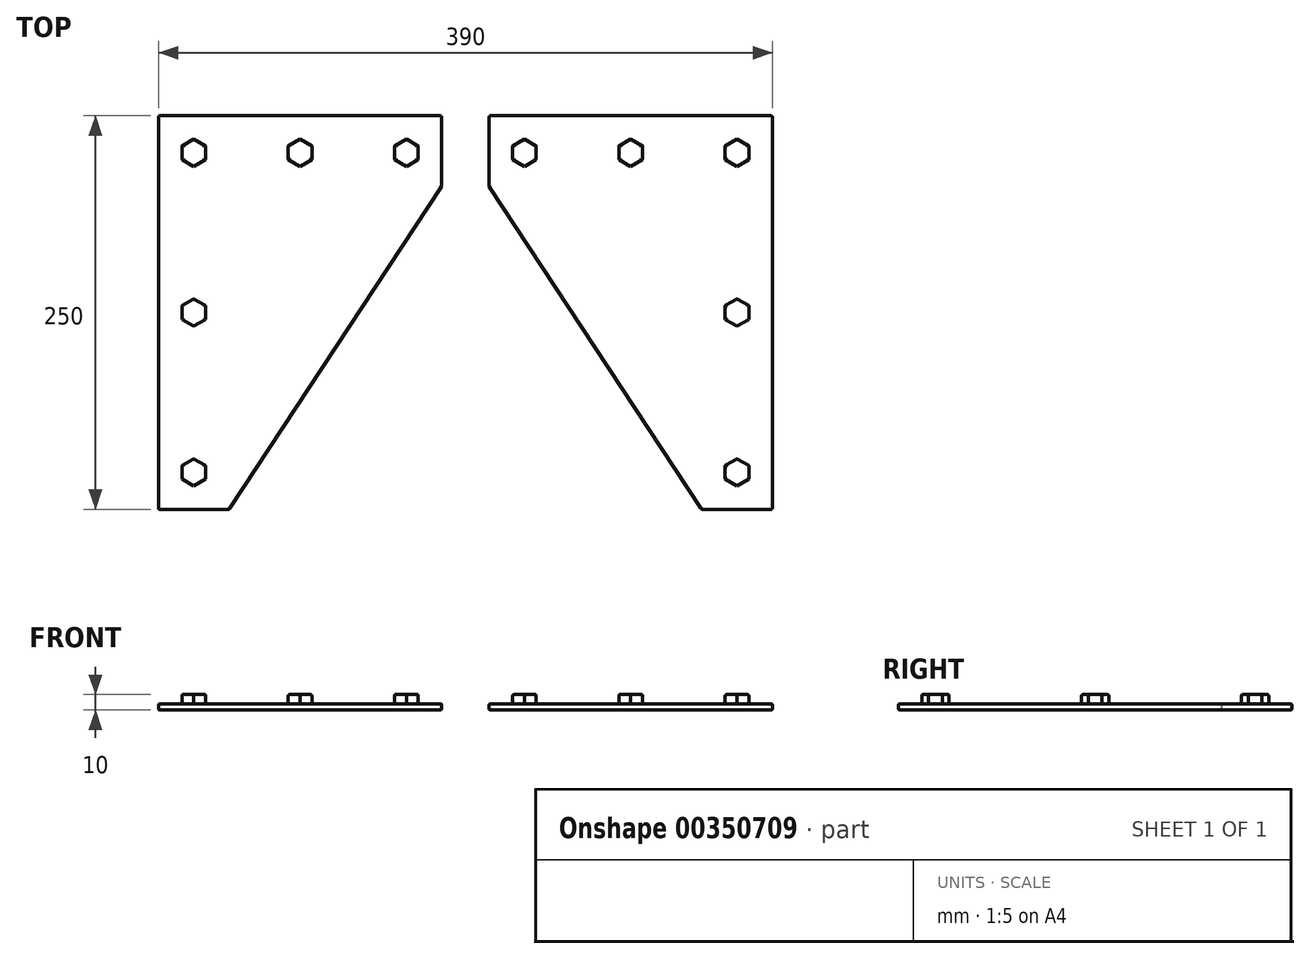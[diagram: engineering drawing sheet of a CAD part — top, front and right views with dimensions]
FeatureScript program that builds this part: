
annotation { "Feature Type Name" : "Feature", "Feature Type Description" : "" }
export const myFeature = defineFeature(function(context is Context, id is Id, definition is map)
    precondition{}
    {
        {
            var Q0;
            Q0=qCreatedBy(makeId("Top.planeOp"),FACE);
            var sketch = newSketch(context, id + "F0", { "sketchPlane" : qUnion([Q0])});
            skLineSegment(sketch, "E0", {"start": v(15, 200) * mm, "end": v(195, 200) * mm});
            skLineSegment(sketch, "E1", {"start": v(195, 200) * mm, "end": v(195, -50) * mm});
            skLineSegment(sketch, "E2", {"start": v(195, -50) * mm, "end": v(150, -50) * mm});
            skLineSegment(sketch, "E3", {"start": v(15, 200) * mm, "end": v(15, 155) * mm});
            skLineSegment(sketch, "E4", {"start": v(15, 155) * mm, "end": v(150, -50) * mm});
            skSolve(sketch);
        }
        {
            var Q0;
            Q0=qSketchRegion(id+"F0",true);
            extrude(context, id + "F1", {"entities" : qUnion([Q0]), "depth" : 4 * mm});
        }
        {
            var Q0;
            Q0=makeQuery(id+"F1.opExtrude","CAP_FACE",FACE,{"disambiguationData":[OSD([sQuery(id+"F0.wireOp",EDGE,"OxDFXuYp-wWxs-4NzO-t9D3-rnYw7JfFts5y"),sQuery(id+"F0.wireOp",EDGE,"E0"),sQuery(id+"F0.wireOp",EDGE,"E1"),sQuery(id+"F0.wireOp",EDGE,"E2")])],"isStart":false});
            var Q1;
            Q1=makeQuery(id+"F1.opExtrude","CAP_FACE",FACE,{"disambiguationData":[OSD([sQuery(id+"F0.wireOp",EDGE,"OxDFXuYp-wWxs-4NzO-t9D3-rnYw7JfFts5y"),sQuery(id+"F0.wireOp",EDGE,"E0"),sQuery(id+"F0.wireOp",EDGE,"E1"),sQuery(id+"F0.wireOp",EDGE,"E2")])],"isStart":true});
            var Q2;
            Q2=makeQuery(id+"F1.opExtrude","SWEPT_EDGE",EDGE,{"disambiguationData":[OSD([sQuery(id+"F0.wireOp",EDGE,"E1"),sQuery(id+"F0.wireOp",EDGE,"E2")])]});
            var Q3;
            Q3=makeQuery(id+"F1.opExtrude","SWEPT_EDGE",EDGE,{"disambiguationData":[OSD([sQuery(id+"F0.wireOp",EDGE,"OxDFXuYp-wWxs-4NzO-t9D3-rnYw7JfFts5y"),sQuery(id+"F0.wireOp",EDGE,"E2")])]});
            var Q4;
            Q4=makeQuery(id+"F1.opExtrude","SWEPT_EDGE",EDGE,{"disambiguationData":[OSD([sQuery(id+"F0.wireOp",EDGE,"E0"),sQuery(id+"F0.wireOp",EDGE,"E1")])]});
            var Q5;
            Q5=makeQuery(id+"F1.opExtrude","SWEPT_EDGE",EDGE,{"disambiguationData":[OSD([sQuery(id+"F0.wireOp",EDGE,"OxDFXuYp-wWxs-4NzO-t9D3-rnYw7JfFts5y"),sQuery(id+"F0.wireOp",EDGE,"E0")])]});
            fillet(context, id + "F2", {"entities" : qUnion([Q0, Q1, Q2, Q3, Q4, Q5]), "radius" : 1 * mm, "tangentPropagation" : true, "allowEdgeOverflow" : false});
        }
        {
            var Q0;
            Q0=makeQuery(id+"F1.opExtrude","CAP_FACE",FACE,{"disambiguationData":[OSD([sQuery(id+"F0.wireOp",EDGE,"OxDFXuYp-wWxs-4NzO-t9D3-rnYw7JfFts5y"),sQuery(id+"F0.wireOp",EDGE,"E0"),sQuery(id+"F0.wireOp",EDGE,"E1"),sQuery(id+"F0.wireOp",EDGE,"E2")])],"isStart":false});
            var sketch = newSketch(context, id + "F3", { "sketchPlane" : qUnion([Q0])});
            skCircle(sketch, "E5.cCircle", {"center": v(37.5, 176.5) * mm, "radius": 7.5 * mm, "construction": true});
            skLineSegment(sketch, "E5.0", {"start": v(45, 172.17) * mm, "end": v(37.5, 167.84) * mm});
            skLineSegment(sketch, "E5.1", {"start": v(37.5, 167.84) * mm, "end": v(30, 172.17) * mm});
            skLineSegment(sketch, "E5.2", {"start": v(30, 172.17) * mm, "end": v(30, 180.83) * mm});
            skLineSegment(sketch, "E5.3", {"start": v(30, 180.83) * mm, "end": v(37.5, 185.16) * mm});
            skLineSegment(sketch, "E5.4", {"start": v(37.5, 185.16) * mm, "end": v(45, 180.83) * mm});
            skLineSegment(sketch, "E5.5", {"start": v(45, 180.83) * mm, "end": v(45, 172.17) * mm});
            skPoint(sketch, "E5.0.midPoint", {"position": v(41.25, 170) * mm});
            skPoint(sketch, "E6.1.0.0", {"position": v(108.75, 170) * mm});
            skCircle(sketch, "E6.1.0.1", {"center": v(105, 176.5) * mm, "radius": 7.5 * mm, "construction": true});
            skLineSegment(sketch, "E6.1.0.2", {"start": v(105, 185.16) * mm, "end": v(112.5, 180.83) * mm});
            skLineSegment(sketch, "E6.1.0.3", {"start": v(112.5, 172.17) * mm, "end": v(105, 167.84) * mm});
            skLineSegment(sketch, "E6.1.0.4", {"start": v(105, 167.84) * mm, "end": v(97.5, 172.17) * mm});
            skLineSegment(sketch, "E6.1.0.5", {"start": v(112.5, 180.83) * mm, "end": v(112.5, 172.17) * mm});
            skLineSegment(sketch, "E6.1.0.6", {"start": v(97.5, 180.83) * mm, "end": v(105, 185.16) * mm});
            skLineSegment(sketch, "E6.1.0.7", {"start": v(97.5, 172.17) * mm, "end": v(97.5, 180.83) * mm});
            skPoint(sketch, "E6.2.0.0", {"position": v(176.25, 170) * mm});
            skCircle(sketch, "E6.2.0.1", {"center": v(172.5, 176.5) * mm, "radius": 7.5 * mm, "construction": true});
            skLineSegment(sketch, "E6.2.0.2", {"start": v(172.5, 185.16) * mm, "end": v(180, 180.83) * mm});
            skLineSegment(sketch, "E6.2.0.3", {"start": v(180, 172.17) * mm, "end": v(172.5, 167.84) * mm});
            skLineSegment(sketch, "E6.2.0.4", {"start": v(172.5, 167.84) * mm, "end": v(165, 172.17) * mm});
            skLineSegment(sketch, "E6.2.0.5", {"start": v(180, 180.83) * mm, "end": v(180, 172.17) * mm});
            skLineSegment(sketch, "E6.2.0.6", {"start": v(165, 180.83) * mm, "end": v(172.5, 185.16) * mm});
            skLineSegment(sketch, "E6.2.0.7", {"start": v(165, 172.17) * mm, "end": v(165, 180.83) * mm});
            skLineSegment(sketch, "E6.direction1", {"start": v(30, 172.17) * mm, "end": v(97.5, 172.17) * mm, "construction": true});
            skCircle(sketch, "E7.0.1.0", {"center": v(172.5, 75) * mm, "radius": 7.5 * mm, "construction": true});
            skLineSegment(sketch, "E7.0.1.1", {"start": v(165, 70.67) * mm, "end": v(165, 79.33) * mm});
            skLineSegment(sketch, "E7.0.1.2", {"start": v(165, 79.33) * mm, "end": v(172.5, 83.66) * mm});
            skLineSegment(sketch, "E7.0.1.3", {"start": v(172.5, 66.34) * mm, "end": v(165, 70.67) * mm});
            skLineSegment(sketch, "E7.0.1.4", {"start": v(180, 70.67) * mm, "end": v(172.5, 66.34) * mm});
            skLineSegment(sketch, "E7.0.1.5", {"start": v(180, 79.33) * mm, "end": v(180, 70.67) * mm});
            skPoint(sketch, "E7.0.1.6", {"position": v(176.25, 68.5) * mm});
            skLineSegment(sketch, "E7.0.1.7", {"start": v(172.5, 83.66) * mm, "end": v(180, 79.33) * mm});
            skCircle(sketch, "E7.0.2.0", {"center": v(172.5, -26.5) * mm, "radius": 7.5 * mm, "construction": true});
            skLineSegment(sketch, "E7.0.2.1", {"start": v(165, -30.83) * mm, "end": v(165, -22.17) * mm});
            skLineSegment(sketch, "E7.0.2.2", {"start": v(165, -22.17) * mm, "end": v(172.5, -17.84) * mm});
            skLineSegment(sketch, "E7.0.2.3", {"start": v(172.5, -35.16) * mm, "end": v(165, -30.83) * mm});
            skLineSegment(sketch, "E7.0.2.4", {"start": v(180, -30.83) * mm, "end": v(172.5, -35.16) * mm});
            skLineSegment(sketch, "E7.0.2.5", {"start": v(180, -22.17) * mm, "end": v(180, -30.83) * mm});
            skPoint(sketch, "E7.0.2.6", {"position": v(176.25, -33) * mm});
            skLineSegment(sketch, "E7.0.2.7", {"start": v(172.5, -17.84) * mm, "end": v(180, -22.17) * mm});
            skLineSegment(sketch, "E7.direction1", {"start": v(165, 172.17) * mm, "end": v(190, 172.17) * mm, "construction": true});
            skLineSegment(sketch, "E7.direction2", {"start": v(165, 172.17) * mm, "end": v(165, 70.67) * mm, "construction": true});
            skSolve(sketch);
        }
        {
            var Q0;
            Q0=qSketchRegion(id+"F3",true);
            extrude(context, id + "F4", {"entities" : qUnion([Q0]), "operationType" : NewBodyOperationType.ADD, "depth" : 6 * mm});
        }
        {
            var Q0;
            Q0=makeQuery(id+"F4.opExtrude","CAP_FACE",FACE,{"disambiguationData":[OSD([sQuery(id+"F3.wireOp",EDGE,"E7.0.2.1"),sQuery(id+"F3.wireOp",EDGE,"E7.0.2.2"),sQuery(id+"F3.wireOp",EDGE,"E7.0.2.3"),sQuery(id+"F3.wireOp",EDGE,"E7.0.2.4"),sQuery(id+"F3.wireOp",EDGE,"E7.0.2.5"),sQuery(id+"F3.wireOp",EDGE,"E7.0.2.7")])],"isStart":false});
            var Q1;
            Q1=makeQuery(id+"F4.opExtrude","CAP_FACE",FACE,{"disambiguationData":[OSD([sQuery(id+"F3.wireOp",EDGE,"E7.0.1.1"),sQuery(id+"F3.wireOp",EDGE,"E7.0.1.2"),sQuery(id+"F3.wireOp",EDGE,"E7.0.1.3"),sQuery(id+"F3.wireOp",EDGE,"E7.0.1.4"),sQuery(id+"F3.wireOp",EDGE,"E7.0.1.5"),sQuery(id+"F3.wireOp",EDGE,"E7.0.1.7")])],"isStart":false});
            var Q2;
            Q2=makeQuery(id+"F4.opExtrude","CAP_FACE",FACE,{"disambiguationData":[OSD([sQuery(id+"F3.wireOp",EDGE,"E6.2.0.2"),sQuery(id+"F3.wireOp",EDGE,"E6.2.0.3"),sQuery(id+"F3.wireOp",EDGE,"E6.2.0.4"),sQuery(id+"F3.wireOp",EDGE,"E6.2.0.5"),sQuery(id+"F3.wireOp",EDGE,"E6.2.0.6"),sQuery(id+"F3.wireOp",EDGE,"E6.2.0.7")])],"isStart":false});
            var Q3;
            Q3=makeQuery(id+"F4.opExtrude","CAP_FACE",FACE,{"disambiguationData":[OSD([sQuery(id+"F3.wireOp",EDGE,"E6.1.0.2"),sQuery(id+"F3.wireOp",EDGE,"E6.1.0.3"),sQuery(id+"F3.wireOp",EDGE,"E6.1.0.4"),sQuery(id+"F3.wireOp",EDGE,"E6.1.0.5"),sQuery(id+"F3.wireOp",EDGE,"E6.1.0.6"),sQuery(id+"F3.wireOp",EDGE,"E6.1.0.7")])],"isStart":false});
            var Q4;
            Q4=makeQuery(id+"F4.opExtrude","CAP_FACE",FACE,{"disambiguationData":[OSD([sQuery(id+"F3.wireOp",EDGE,"E5.0"),sQuery(id+"F3.wireOp",EDGE,"E5.1"),sQuery(id+"F3.wireOp",EDGE,"E5.2"),sQuery(id+"F3.wireOp",EDGE,"E5.3"),sQuery(id+"F3.wireOp",EDGE,"E5.4"),sQuery(id+"F3.wireOp",EDGE,"E5.5")])],"isStart":false});
            fillet(context, id + "F5", {"entities" : qUnion([Q0, Q1, Q2, Q3, Q4]), "radius" : 1 * mm, "tangentPropagation" : true, "allowEdgeOverflow" : false});
        }
        {
            var Q0;
            Q0=makeQuery(id+"F1.opExtrude","SWEPT_BODY",BODY,{"disambiguationData":[OSD([sQuery(id+"F0.wireOp",EDGE,"E0"),sQuery(id+"F0.wireOp",EDGE,"E1"),sQuery(id+"F0.wireOp",EDGE,"E2"),sQuery(id+"F0.wireOp",EDGE,"E3"),sQuery(id+"F0.wireOp",EDGE,"E4")])]});
            var Q1;
            Q1=qCreatedBy(makeId("Right.planeOp"),FACE);
            mirror(context, id + "F6", {"entities" : qUnion([Q0]), "mirrorPlane" : qUnion([Q1])});
        }
    });
